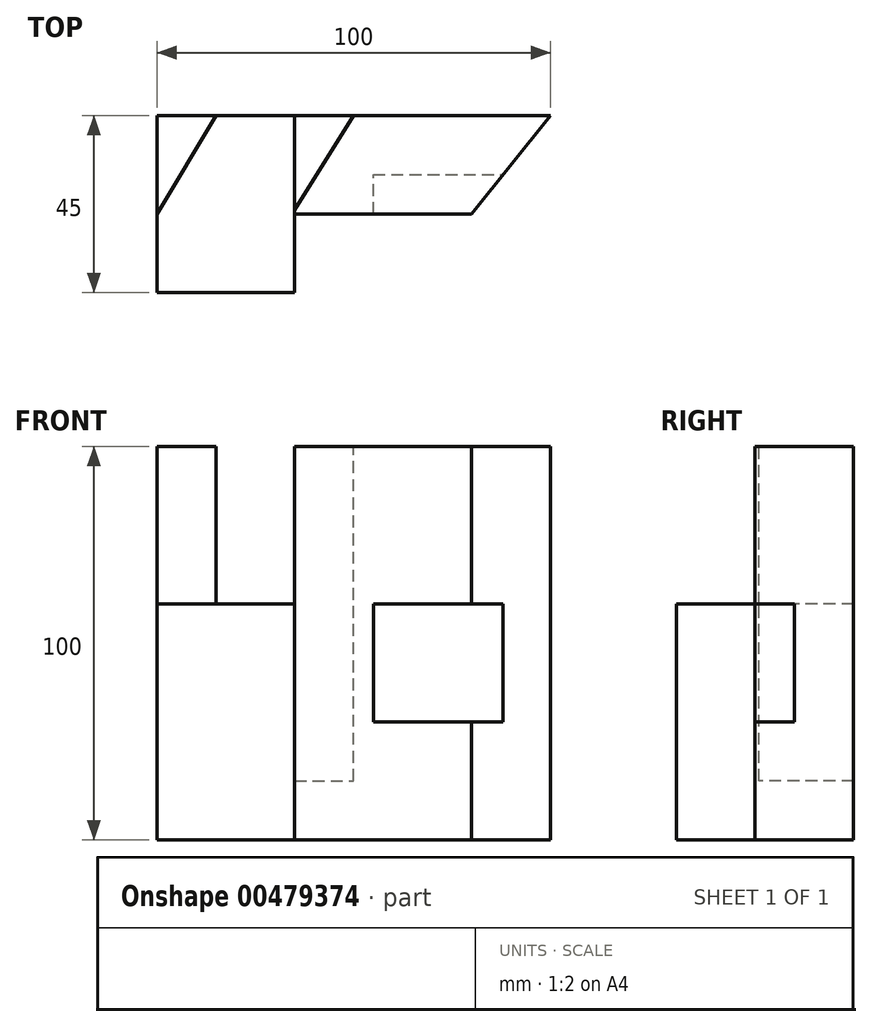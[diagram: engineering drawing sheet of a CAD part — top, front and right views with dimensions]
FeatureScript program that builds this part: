
annotation { "Feature Type Name" : "Feature", "Feature Type Description" : "" }
export const myFeature = defineFeature(function(context is Context, id is Id, definition is map)
    precondition{}
    {
        {
            var Q0;
            Q0=qCreatedBy(makeId("Top.planeOp"),FACE);
            var sketch = newSketch(context, id + "F0", { "sketchPlane" : qUnion([Q0])});
            skLineSegment(sketch, "E0.bottom", {"start": v(0, 0) * mm, "end": v(100, 0) * mm});
            skLineSegment(sketch, "E0.top", {"start": v(0, 45) * mm, "end": v(100, 45) * mm});
            skLineSegment(sketch, "E0.left", {"start": v(0, 0) * mm, "end": v(0, 45) * mm});
            skLineSegment(sketch, "E0.right", {"start": v(100, 0) * mm, "end": v(100, 45) * mm});
            skSolve(sketch);
        }
        {
            var Q0;
            Q0 = qSketchRegion(id + "F0", true);
            extrude(context, id + "F1", {"entities" : qUnion([Q0]), "depth" : 100 * mm});
        }
        {
            var Q0;
            Q0=makeQuery(id+"F1.opExtrude","CAP_FACE",FACE,{"disambiguationData":[OSD([sQuery(id+"F0.wireOp",EDGE,"E0.bottom"),sQuery(id+"F0.wireOp",EDGE,"E0.top"),sQuery(id+"F0.wireOp",EDGE,"E0.left"),sQuery(id+"F0.wireOp",EDGE,"E0.right")])],"isStart":false});
            var sketch = newSketch(context, id + "F2", { "sketchPlane" : qUnion([Q0])});
            skLineSegment(sketch, "E1.bottom", {"start": v(100, 0) * mm, "end": v(35, 0) * mm});
            skLineSegment(sketch, "E1.top", {"start": v(100, 20) * mm, "end": v(35, 20) * mm});
            skLineSegment(sketch, "E1.left", {"start": v(100, 0) * mm, "end": v(100, 20) * mm});
            skLineSegment(sketch, "E1.right", {"start": v(35, 0) * mm, "end": v(35, 20) * mm});
            skSolve(sketch);
        }
        {
            var Q0;
            Q0 = qSketchRegion(id + "F2", true);
            extrude(context, id + "F3", {"entities" : qUnion([Q0]), "operationType" : NewBodyOperationType.REMOVE, "endBound" : BoundingType.THROUGH_ALL, "oppositeDirection" : true, "depth" : 25 * mm});
        }
        {
            var Q0;
            Q0=makeQuery(id+"F1.opExtrude","SWEPT_FACE",FACE,{"disambiguationData":[OSD([sQuery(id+"F0.wireOp",EDGE,"E0.bottom")])]});
            var sketch = newSketch(context, id + "F4", { "sketchPlane" : qUnion([Q0])});
            skLineSegment(sketch, "E2.bottom", {"start": v(0, 100) * mm, "end": v(35, 100) * mm});
            skLineSegment(sketch, "E2.top", {"start": v(0, 60) * mm, "end": v(35, 60) * mm});
            skLineSegment(sketch, "E2.left", {"start": v(0, 100) * mm, "end": v(0, 60) * mm});
            skLineSegment(sketch, "E2.right", {"start": v(35, 100) * mm, "end": v(35, 60) * mm});
            skSolve(sketch);
        }
        {
            var Q0;
            Q0 = qSketchRegion(id + "F4", true);
            extrude(context, id + "F5", {"entities" : qUnion([Q0]), "operationType" : NewBodyOperationType.REMOVE, "endBound" : BoundingType.THROUGH_ALL, "oppositeDirection" : true, "depth" : 25 * mm});
        }
        {
            var Q0;
            Q0=makeQuery(id+"F5.boolean.opBoolean","COPY",FACE,{"derivedFrom":makeQuery(id+"F5.opExtrude","SWEPT_FACE",FACE,{"disambiguationData":[OSD([sQuery(id+"F4.wireOp",EDGE,"E2.top")])]})});
            var sketch = newSketch(context, id + "F6", { "sketchPlane" : qUnion([Q0])});
            skLineSegment(sketch, "E3", {"start": v(15, 45) * mm, "end": v(0, 20) * mm});
            skSolve(sketch);
        }
        {
            var Q0;
            Q0 = qSketchRegion(id + "F6", true);
            var Q1;
            {var subQ0=sQuery(id+"F6.wireOp",EDGE,"E3");Q1=makeQuery(id+"F6.imprint","IMPRINT",FACE,{"disambiguationData":[TD([[makeQuery(id+"F6.imprint","IMPRINT",EDGE,{"derivedFrom":subQ0}),-1.0]])]});}
            extrude(context, id + "F7", {"entities" : qUnion([Q0, Q1]), "operationType" : NewBodyOperationType.ADD, "depth" : 40 * mm});
        }
        {
            var Q0;
            Q0=makeQuery(id+"F1.opExtrude","CAP_FACE",FACE,{"disambiguationData":[OSD([sQuery(id+"F0.wireOp",EDGE,"E0.bottom"),sQuery(id+"F0.wireOp",EDGE,"E0.top"),sQuery(id+"F0.wireOp",EDGE,"E0.left"),sQuery(id+"F0.wireOp",EDGE,"E0.right")])],"isStart":false});
            var sketch = newSketch(context, id + "F8", { "sketchPlane" : qUnion([Q0])});
            skLineSegment(sketch, "E4", {"start": v(50, 45) * mm, "end": v(35, 21) * mm});
            skSolve(sketch);
        }
        {
            var Q0;
            {var subQ0=sQuery(id+"F8.wireOp",EDGE,"E4");Q0=makeQuery(id+"F8.imprint","IMPRINT",FACE,{"disambiguationData":[TD([[makeQuery(id+"F8.imprint","IMPRINT",EDGE,{"derivedFrom":subQ0}),-1.0]])]});}
            extrude(context, id + "F9", {"entities" : qUnion([Q0]), "operationType" : NewBodyOperationType.REMOVE, "oppositeDirection" : true, "depth" : 85 * mm});
        }
        {
            var Q0;
            Q0=makeQuery(id+"F1.opExtrude","CAP_FACE",FACE,{"disambiguationData":[OSD([sQuery(id+"F0.wireOp",EDGE,"E0.bottom"),sQuery(id+"F0.wireOp",EDGE,"E0.top"),sQuery(id+"F0.wireOp",EDGE,"E0.left"),sQuery(id+"F0.wireOp",EDGE,"E0.right")])],"isStart":false});
            var sketch = newSketch(context, id + "F10", { "sketchPlane" : qUnion([Q0])});
            skLineSegment(sketch, "E5.bottom", {"start": v(55, 20) * mm, "end": v(88, 20) * mm});
            skLineSegment(sketch, "E5.top", {"start": v(55, 30) * mm, "end": v(88, 30) * mm});
            skLineSegment(sketch, "E5.left", {"start": v(55, 20) * mm, "end": v(55, 30) * mm});
            skLineSegment(sketch, "E5.right", {"start": v(88, 20) * mm, "end": v(88, 30) * mm});
            skSolve(sketch);
        }
        {
            var Q0;
            Q0 = qSketchRegion(id + "F10", true);
            extrude(context, id + "F11", {"entities" : qUnion([Q0]), "operationType" : NewBodyOperationType.REMOVE, "oppositeDirection" : true, "depth" : 70 * mm});
        }
        {
            var Q0;
            Q0=makeQuery(id+"F11.boolean.opBoolean","COPY",FACE,{"derivedFrom":makeQuery(id+"F11.opExtrude","SWEPT_FACE",FACE,{"disambiguationData":[OSD([sQuery(id+"F10.wireOp",EDGE,"E5.top")])]})});
            var sketch = newSketch(context, id + "F12", { "sketchPlane" : qUnion([Q0])});
            skLineSegment(sketch, "E6.bottom", {"start": v(55, 100) * mm, "end": v(88, 100) * mm});
            skLineSegment(sketch, "E6.top", {"start": v(55, 60) * mm, "end": v(88, 60) * mm});
            skLineSegment(sketch, "E6.left", {"start": v(55, 100) * mm, "end": v(55, 60) * mm});
            skLineSegment(sketch, "E6.right", {"start": v(88, 100) * mm, "end": v(88, 60) * mm});
            skSolve(sketch);
        }
        {
            var Q0;
            Q0=makeQuery(id+"F12.imprint","IMPRINT",FACE,{"disambiguationData":[TD([[makeQuery(id+"F12.imprint","IMPRINT",EDGE,{"derivedFrom":sQuery(id+"F12.wireOp",EDGE,"E6.bottom")}),-1.0]])]});
            extrude(context, id + "F13", {"entities" : qUnion([Q0]), "operationType" : NewBodyOperationType.ADD, "depth" : 10 * mm});
        }
        {
            var Q0;
            Q0=makeQuery(id+"F1.opExtrude","CAP_FACE",FACE,{"disambiguationData":[OSD([sQuery(id+"F0.wireOp",EDGE,"E0.bottom"),sQuery(id+"F0.wireOp",EDGE,"E0.top"),sQuery(id+"F0.wireOp",EDGE,"E0.left"),sQuery(id+"F0.wireOp",EDGE,"E0.right")])],"isStart":false});
            var sketch = newSketch(context, id + "F14", { "sketchPlane" : qUnion([Q0])});
            skLineSegment(sketch, "E7", {"start": v(100, 45) * mm, "end": v(80, 20) * mm});
            skSolve(sketch);
        }
        {
            var Q0;
            Q0 = qSketchRegion(id + "F14", true);
            var Q1;
            {var subQ0=sQuery(id+"F14.wireOp",EDGE,"E7");Q1=makeQuery(id+"F14.imprint","IMPRINT",FACE,{"disambiguationData":[TD([[makeQuery(id+"F14.imprint","IMPRINT",EDGE,{"derivedFrom":subQ0}),1.0]])]});}
            extrude(context, id + "F15", {"entities" : qUnion([Q0, Q1]), "operationType" : NewBodyOperationType.REMOVE, "endBound" : BoundingType.THROUGH_ALL, "oppositeDirection" : true, "depth" : 25 * mm});
        }
    });
